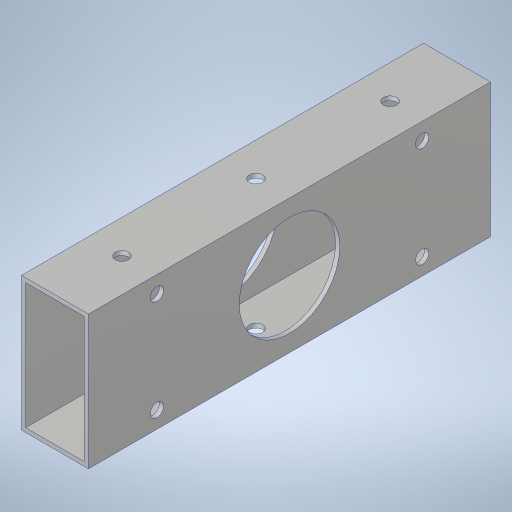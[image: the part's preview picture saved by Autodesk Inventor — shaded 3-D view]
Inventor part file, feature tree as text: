
AUTODESK INVENTOR PART (.ipt)
format: ipt  version: 2023.4 (Build 274418000, 418)  size: 261,120 bytes
history: native  units: in
note: dims shown in document units (in); Inventor stores cm internally (conversion verified against a paired STEP export)
features: sketch x4, hole x3, extrude x2, projected_geometry x1
ambient origin geometry x8: Origin, YZ Plane, XZ Plane, XY Plane, X Axis, Y Axis, Z Axis, Center Point
bodies: Solid1 (feature_tree)
feature tree (10):
  extrude  "Extrusion1"  Depth=4.0in
  hole  "Hole1"  [1 undecoded]
  hole  "Hole3"  [1 undecoded]
  extrude  "Extrusion2"  Depth=1.0in
  hole  "Hole2"  [1 undecoded]
  sketch  "Sketch2"  dims[d4=0.0in d5=4.0in]
  projected_geometry  "Projected Loop1"
  sketch  "Sketch3"  dims[d6=0.201in d7=0.75in d8=0.385in d9=0.25in d10=0.5635in d11=1.0in d12=0.8108in d14=4.7244in]
  sketch  "Sketch4"  dims[d15=3.7402in d16=4.2323in]
  sketch  "Sketch5"  dims[d17=1.5in d18=0.156in d19=0.38in d20=0.375in d21=0.25in d22=0.5635in d23=1.0in d24=0.8108in d25=4.2323in d28=1.5in d29=0.201in d30=0.38in d31=0.385in d32=0.25in d33=0.5635in d34=1.0in d35=0.8108in d36=1.5in d37=1.0in d38=0.0in]
note: 3 required parameter values undecoded (feature->parameter linkage not recoverable at this tier; creation-order binding heuristic only, values carry confidence <= 0.55)
